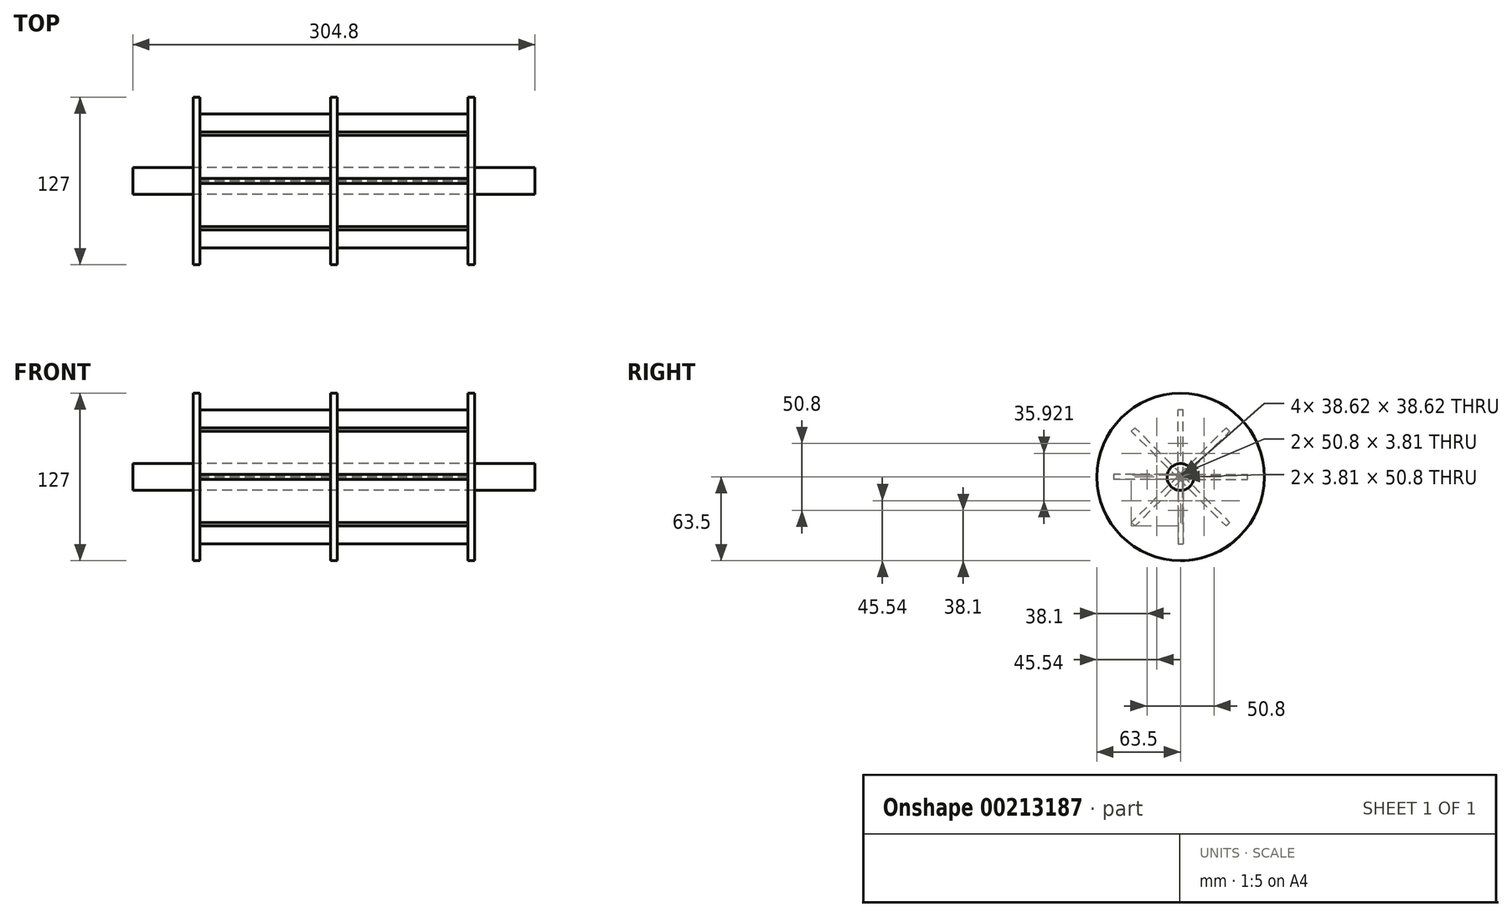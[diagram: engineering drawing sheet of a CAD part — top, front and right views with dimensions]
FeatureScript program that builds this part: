
annotation { "Feature Type Name" : "Feature", "Feature Type Description" : "" }
export const myFeature = defineFeature(function(context is Context, id is Id, definition is map)
    precondition{}
    {
        {
            var Q0;
            Q0=qCreatedBy(makeId("Right.planeOp"),FACE);
            var sketch = newSketch(context, id + "F0", { "sketchPlane" : qUnion([Q0])});
            skCircle(sketch, "E0", {"center": v(0, 0) * mm, "radius": 63.5 * mm});
            skSolve(sketch);
        }
        {
            var Q0;
            Q0=makeQuery(id+"F0.imprint","IMPRINT",FACE,{"disambiguationData":[TD([[makeQuery(id+"F0.imprint","IMPRINT",EDGE,{"derivedFrom":sQuery(id+"F0.wireOp",EDGE,"E0")}),1.0]])]});
            extrude(context, id + "F1", {"entities" : qUnion([Q0]), "endBound" : BoundingType.SYMMETRIC, "depth" : 5.08 * mm});
        }
        {
            var Q0;
            Q0=qCreatedBy(makeId("Right.planeOp"),FACE);
            var sketch = newSketch(context, id + "F2", { "sketchPlane" : qUnion([Q0])});
            skLineSegment(sketch, "E1.bottom", {"start": v(-1.9, 50.8) * mm, "end": v(1.9, 50.8) * mm});
            skLineSegment(sketch, "E1.top", {"start": v(-1.9, 0) * mm, "end": v(1.9, 0) * mm});
            skLineSegment(sketch, "E1.left", {"start": v(-1.9, 50.8) * mm, "end": v(-1.9, 0) * mm});
            skLineSegment(sketch, "E1.right", {"start": v(1.9, 50.8) * mm, "end": v(1.9, 0) * mm});
            skSolve(sketch);
        }
        {
            var Q0;
            Q0=qSketchRegion(id+"F2",true);
            extrude(context, id + "F3", {"entities" : qUnion([Q0]), "operationType" : NewBodyOperationType.ADD, "endBound" : BoundingType.SYMMETRIC, "depth" : 203.2 * mm});
        }
        {
            var Q0;
            Q0=qCreatedBy(makeId("Front.planeOp"),FACE);
            var sketch = newSketch(context, id + "F4", { "sketchPlane" : qUnion([Q0])});
            skLineSegment(sketch, "E2", {"start": v(-68.39, 0) * mm, "end": v(69.79, 0) * mm, "construction": true});
            skSolve(sketch);
        }
        {
            var Q0;
            Q0=makeQuery(id+"F1.opExtrude","SWEPT_BODY",BODY,{"disambiguationData":[OSD([sQuery(id+"F0.wireOp",EDGE,"E0")])]});
            var Q1;
            Q1=sQuery(id+"F4.wireOp",EDGE,"E2");
            circularPattern(context, id + "F5", {"entities" : qUnion([Q0]), "axis" : qUnion([Q1]), "angle" : 360 * degree, "instanceCount" : 8, "equalSpace" : true});
        }
        {
            var Q0;
            Q0=makeQuery(id+"F5.opPattern","COPY",FACE,{"derivedFrom":makeQuery(id+"F3.opExtrude","CAP_FACE",FACE,{"disambiguationData":[OSD([sQuery(id+"F2.wireOp",EDGE,"E1.bottom"),sQuery(id+"F2.wireOp",EDGE,"E1.top"),sQuery(id+"F2.wireOp",EDGE,"E1.left"),sQuery(id+"F2.wireOp",EDGE,"E1.right")])],"isStart":false}),"instanceName":"6"});
            var sketch = newSketch(context, id + "F6", { "sketchPlane" : qUnion([Q0])});
            skCircle(sketch, "E3", {"center": v(0, 0) * mm, "radius": 63.5 * mm});
            skSolve(sketch);
        }
        {
            var Q0;
            Q0=makeQuery(id+"F6.imprint","IMPRINT",FACE,{"disambiguationData":[TD([[makeQuery(id+"F6.imprint","IMPRINT",EDGE,{"derivedFrom":sQuery(id+"F6.wireOp",EDGE,"E3")}),1.0]])]});
            var Q1;
            Q1=makeQuery(id+"F6.imprint","IMPRINT",FACE,{"disambiguationData":[TD([[makeQuery(id+"F6.imprint","IMPRINT",EDGE,{"derivedFrom":makeQuery(id+"F5.opPattern","COPY",EDGE,{"derivedFrom":makeQuery(id+"F3.opExtrude","CAP_EDGE",EDGE,{"disambiguationData":[OSD([sQuery(id+"F2.wireOp",EDGE,"E1.bottom")])],"isStart":false}),"instanceName":"6"})}),-1.0]])]});
            extrude(context, id + "F7", {"entities" : qUnion([Q0, Q1]), "depth" : 5.08 * mm});
        }
        {
            var Q0;
            Q0=makeQuery(id+"F7.opExtrude","SWEPT_BODY",BODY,{"disambiguationData":[OSD([sQuery(id+"F6.wireOp",EDGE,"E3")])]});
            var Q1;
            Q1=qCreatedBy(makeId("Right.planeOp"),FACE);
            mirror(context, id + "F8", {"entities" : qUnion([Q0]), "mirrorPlane" : qUnion([Q1])});
        }
        {
            var Q0;
            Q0=qCreatedBy(makeId("Right.planeOp"),FACE);
            var sketch = newSketch(context, id + "F9", { "sketchPlane" : qUnion([Q0])});
            skCircle(sketch, "E4", {"center": v(0, 0) * mm, "radius": 10.16 * mm});
            skSolve(sketch);
        }
        {
            var Q0;
            Q0=qSketchRegion(id+"F9",true);
            extrude(context, id + "F10", {"entities" : qUnion([Q0]), "endBound" : BoundingType.SYMMETRIC, "depth" : 304.8 * mm});
        }
    });
